# Revit family: Jumbo 40M Exit Wall Hosted R18
name_source: partatom
category: Lighting Fixtures
revit_build: Autodesk Revit 2018 (Build: 20170223_1515(x64)
units: mm (PartAtom-declared; Revit-internal decimal feet)

## family parameters
Always vertical = Yes
Cut with Voids When Loaded = No
Host = Wall
Light Source = Yes
OmniClass Number = 23.80.70.00
OmniClass Title = Lighting
Part Type = Normal
Room Calculation Point = No
Round Connector Dimension = Use Diameter
Shared = No

## types (1)
- LJELED-WM-R
    AS2293 Classification = C0=D6.3 C90=E3.2
    Battery = 1530010	BATTERY:L10 3.3V 2.5AH 200mm lead, BRKT.
    Battery type = Lithium Nanophosphate, 3.3V 2500mAh

Lithium Nanophosphate, 3.3V 2500mAh

Lithium Nanophosphate, 3.3V 2500mAh

Lithium Nanophosphate 3.3V 2500mAh
    Charger Method = Lithium Nanophosphate, 3.3V 2500mAh

Lithium Nanophosphate, 3.3V 2500mAh

Intelligent Current Limited Constant Voltage
    Color Filter = 16777215
    Construction = Powder coated Metal Frame with Acrylic Diffuser
    Dimensions = 630mm x 100mm x 320mm
    Dimming Lamp Color Temperature Shift = <None>
    Emit Shape Visible in Rendering = No
    Emit from Rectangle Length = 1219 mm
    Emit from Rectangle Width = 610 mm
    IP Rating = IP20
    Inverter/Charger = LJELED-40-CKIT-110	Jumbo LED Exit, Control Kit, L10
    Lamp = 12 x High Intensity LED, Surface Mounted onto a replaceable lamp bar - 100,000hrs
    Mounting = Surface Mount
    Operating Mode = Maintained
    Operating Temperature = 1˚C to 40˚C
    Operating Voltage = 240V AC; 50Hz
    Photometric Web File = ll19642 - LJELED-40-CM-ZW (One-box Solution 110mA).IES
    Power Consumption = 3.2 Watts (Standby), 5.6 Watts (Max)
    Product Description = L10 Optimum Jumbo Emergency Exit
    Replacement Lamp = 8002470	PCA:Duris E5 Strip for LJELED.CT10050-D1
    Testing Mode = Manual Test Switch
    Tilt Angle = 60.00°
    Viewing Distance = 40M

## geometry (parser evidence)
native form markers: Sweep x2
no freeform markers — native parametric forms only
